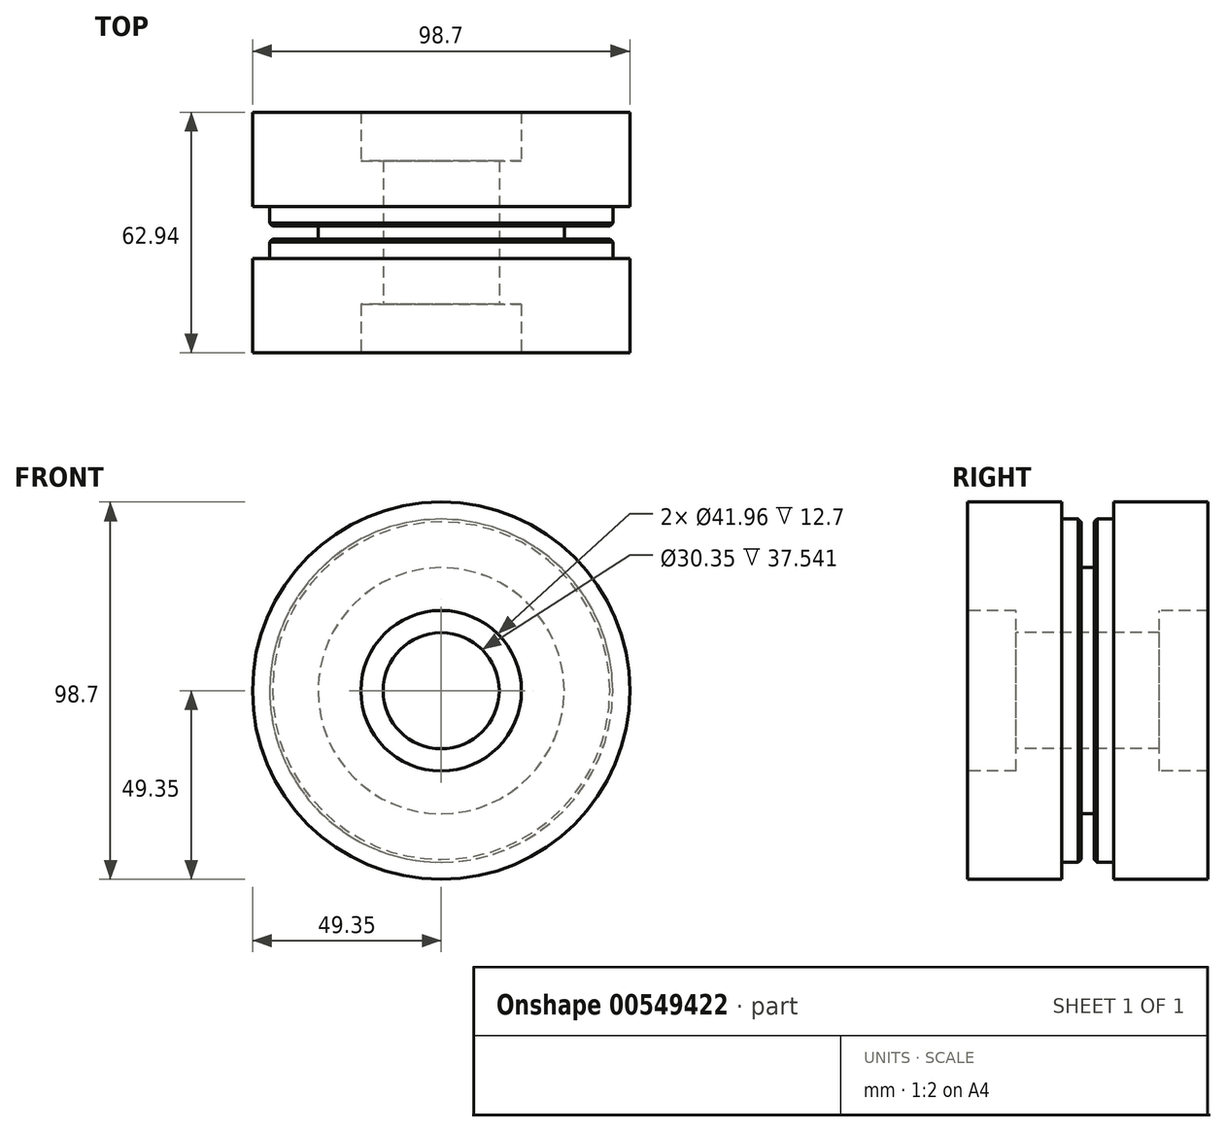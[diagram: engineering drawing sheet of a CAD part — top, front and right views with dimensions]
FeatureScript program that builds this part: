
annotation { "Feature Type Name" : "Feature", "Feature Type Description" : "" }
export const myFeature = defineFeature(function(context is Context, id is Id, definition is map)
    precondition{}
    {
        {
            var Q0;
            Q0=qCreatedBy(makeId("Right.planeOp"),FACE);
            var sketch = newSketch(context, id + "F0", { "sketchPlane" : qUnion([Q0])});
            skLineSegment(sketch, "E0", {"start": v(-35.21, 0) * mm, "end": v(33.24, 0) * mm, "construction": true});
            skLineSegment(sketch, "E1", {"start": v(0, 15.18) * mm, "end": v(-18.77, 15.18) * mm});
            skLineSegment(sketch, "E2", {"start": v(-18.77, 15.18) * mm, "end": v(-18.77, 20.98) * mm});
            skLineSegment(sketch, "E3", {"start": v(-18.77, 20.98) * mm, "end": v(-31.47, 20.98) * mm});
            skLineSegment(sketch, "E4", {"start": v(-31.47, 20.98) * mm, "end": v(-31.47, 49.35) * mm});
            skLineSegment(sketch, "E5", {"start": v(-31.47, 49.35) * mm, "end": v(-6.8, 49.35) * mm});
            skLineSegment(sketch, "E6", {"start": v(-6.8, 49.35) * mm, "end": v(-6.8, 44.88) * mm});
            skLineSegment(sketch, "E7", {"start": v(-6.8, 44.88) * mm, "end": v(-1.71, 44.88) * mm});
            skLineSegment(sketch, "E8", {"start": v(0, 44.88) * mm, "end": v(0, 15.18) * mm, "construction": true});
            skLineSegment(sketch, "E9.MirrorCS", {"start": v(6.8, 44.88) * mm, "end": v(1.71, 44.88) * mm});
            skLineSegment(sketch, "E10.MirrorCS", {"start": v(6.8, 49.35) * mm, "end": v(6.8, 44.88) * mm});
            skLineSegment(sketch, "E11.MirrorCS", {"start": v(31.47, 49.35) * mm, "end": v(6.8, 49.35) * mm});
            skLineSegment(sketch, "E12.MirrorCS", {"start": v(31.47, 20.98) * mm, "end": v(31.47, 49.35) * mm});
            skLineSegment(sketch, "E13.MirrorCS", {"start": v(18.77, 20.98) * mm, "end": v(31.47, 20.98) * mm});
            skLineSegment(sketch, "E14.MirrorCS", {"start": v(18.77, 15.18) * mm, "end": v(18.77, 20.98) * mm});
            skLineSegment(sketch, "E15.MirrorCS", {"start": v(0, 15.18) * mm, "end": v(18.77, 15.18) * mm});
            skLineSegment(sketch, "E16", {"start": v(-1.71, 44.88) * mm, "end": v(-1.71, 32.18) * mm});
            skLineSegment(sketch, "E17", {"start": v(-1.71, 32.18) * mm, "end": v(1.71, 32.18) * mm});
            skLineSegment(sketch, "E18", {"start": v(1.71, 32.18) * mm, "end": v(1.71, 44.88) * mm});
            skPoint(sketch, "E19.orphan", {"position": v(0, 44.88) * mm});
            skSolve(sketch);
        }
        {
            var Q0;
            Q0 = qSketchRegion(id + "F0", true);
            var Q1;
            Q1=sQuery(id+"F0.wireOp",EDGE,"E0");
            revolve(context, id + "F1", {"entities" : qUnion([Q0]), "axis" : qUnion([Q1]), "revolveType" : RevolveType.FULL});
        }
        {
            var Q0;
            Q0=makeQuery(id+"F1.opRevolve","SWEPT_EDGE",EDGE,{"disambiguationData":[OSD([sQuery(id+"F0.wireOp",EDGE,"E9.MirrorCS"),sQuery(id+"F0.wireOp",EDGE,"E18")])]});
            var Q1;
            Q1=makeQuery(id+"F1.opRevolve","SWEPT_EDGE",EDGE,{"disambiguationData":[OSD([sQuery(id+"F0.wireOp",EDGE,"E7"),sQuery(id+"F0.wireOp",EDGE,"E16")])]});
            chamfer(context, id + "F2", {"entities" : qUnion([Q0, Q1]), "width" : 0.76 * mm, "tangentPropagation" : true});
        }
        {
            var Q0;
            Q0=makeQuery(id+"F1.opRevolve","SWEPT_EDGE",EDGE,{"disambiguationData":[OSD([sQuery(id+"F0.wireOp",EDGE,"E16"),sQuery(id+"F0.wireOp",EDGE,"E17")])]});
            var Q1;
            Q1=makeQuery(id+"F1.opRevolve","SWEPT_EDGE",EDGE,{"disambiguationData":[OSD([sQuery(id+"F0.wireOp",EDGE,"E17"),sQuery(id+"F0.wireOp",EDGE,"E18")])]});
            fillet(context, id + "F3", {"entities" : qUnion([Q0, Q1]), "radius" : 0.25 * mm, "tangentPropagation" : true, "allowEdgeOverflow" : false});
        }
    });
